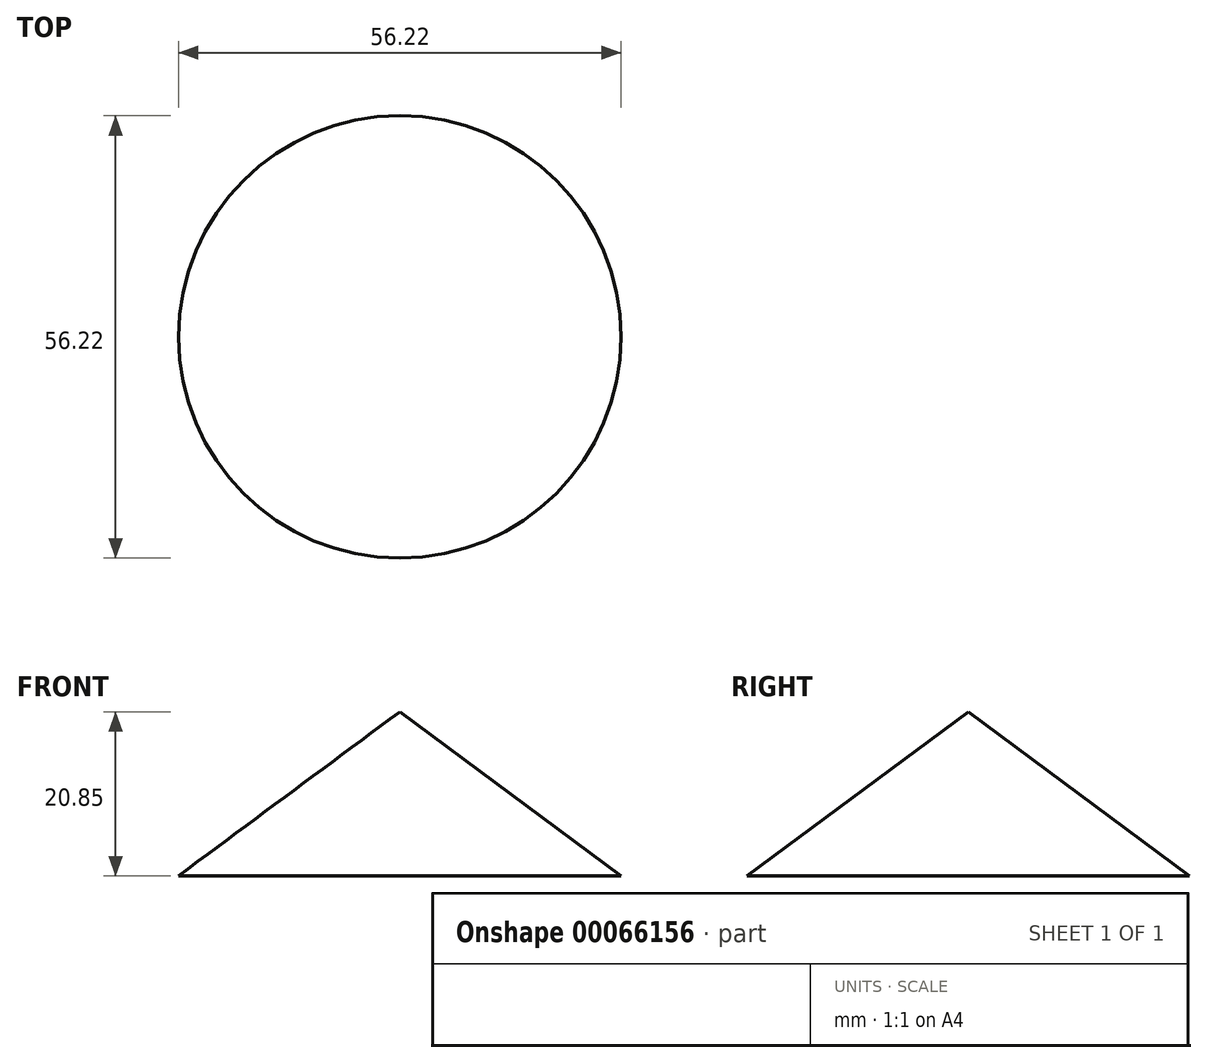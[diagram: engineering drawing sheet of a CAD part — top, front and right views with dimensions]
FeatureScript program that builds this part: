
annotation { "Feature Type Name" : "Feature", "Feature Type Description" : "" }
export const myFeature = defineFeature(function(context is Context, id is Id, definition is map)
    precondition{}
    {
        {
            var Q0;
            Q0=qCreatedBy(makeId("Front.planeOp"),FACE);
            var sketch = newSketch(context, id + "F0", { "sketchPlane" : qUnion([Q0])});
            skLineSegment(sketch, "E0", {"start": v(-28.1, 36.95) * mm, "end": v(0, 36.95) * mm});
            skLineSegment(sketch, "E1", {"start": v(0, 36.95) * mm, "end": v(0, 7.93) * mm});
            skLineSegment(sketch, "E2", {"start": v(0, 7.93) * mm, "end": v(-29.47, 7.93) * mm});
            skLineSegment(sketch, "E3", {"start": v(-29.47, 7.93) * mm, "end": v(-28.1, 36.95) * mm});
            skLineSegment(sketch, "E4", {"start": v(-28.1, 36.95) * mm, "end": v(0, 57.8) * mm});
            skLineSegment(sketch, "E5", {"start": v(0, 57.8) * mm, "end": v(0, 7.93) * mm});
            skSolve(sketch);
        }
        {
            var Q0;
            {var subQ0=sQuery(id+"F0.wireOp",EDGE,"E0");Q0=makeQuery(id+"F0.imprint","IMPRINT",FACE,{"disambiguationData":[TD([[makeQuery(id+"F0.imprint","IMPRINT",EDGE,{"derivedFrom":subQ0}),1.0]])]});}
            var Q1;
            Q1=sQuery(id+"F0.wireOp",EDGE,"E5");
            revolve(context, id + "F1", {"entities" : qUnion([Q0]), "axis" : qUnion([Q1]), "revolveType" : RevolveType.FULL});
        }
    });
